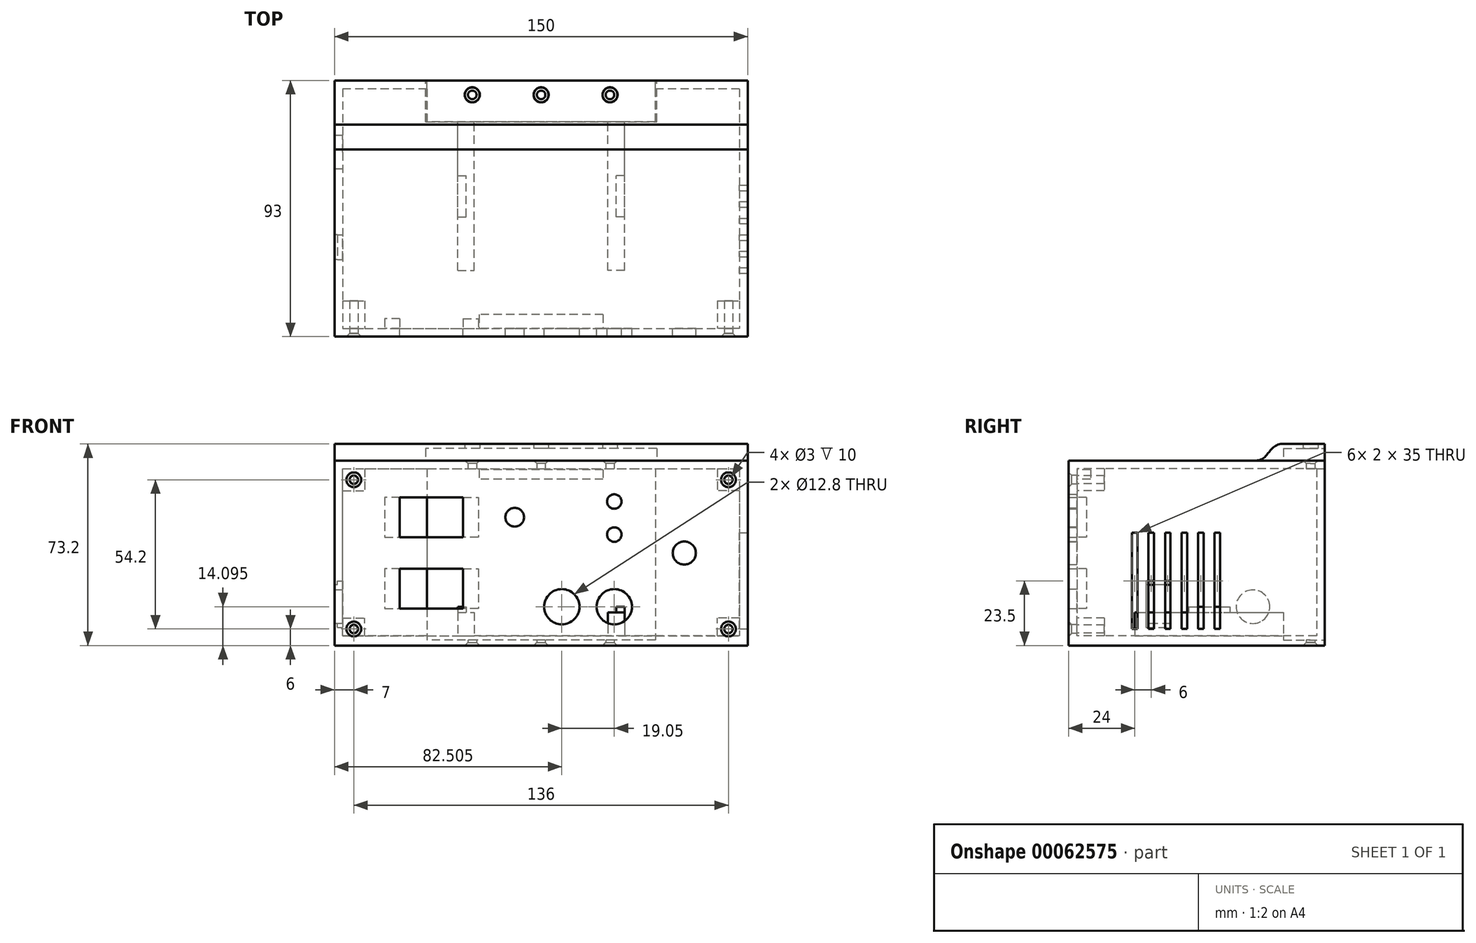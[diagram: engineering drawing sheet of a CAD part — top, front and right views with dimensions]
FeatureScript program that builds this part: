
annotation { "Feature Type Name" : "Feature", "Feature Type Description" : "" }
export const myFeature = defineFeature(function(context is Context, id is Id, definition is map)
    precondition{}
    {
        {
            var Q0;
            Q0=qCreatedBy(makeId("Top.planeOp"),FACE);
            var sketch = newSketch(context, id + "F0", { "sketchPlane" : qUnion([Q0])});
            skLineSegment(sketch, "E0.bottom", {"start": v(-75, 45) * mm, "end": v(75, 45) * mm});
            skLineSegment(sketch, "E0.top", {"start": v(-75, -45) * mm, "end": v(75, -45) * mm});
            skLineSegment(sketch, "E0.left", {"start": v(-75, 45) * mm, "end": v(-75, -45) * mm});
            skLineSegment(sketch, "E0.right", {"start": v(75, 45) * mm, "end": v(75, -45) * mm});
            skLineSegment(sketch, "E1", {"start": v(0, 0) * mm, "end": v(-75, 45) * mm, "construction": true});
            skLineSegment(sketch, "E2", {"start": v(0, 0) * mm, "end": v(-75, -45) * mm, "construction": true});
            skLineSegment(sketch, "E3", {"start": v(0, 0) * mm, "end": v(75, -45) * mm, "construction": true});
            skLineSegment(sketch, "E4", {"start": v(0, 0) * mm, "end": v(75, 45) * mm, "construction": true});
            skSolve(sketch);
        }
        {
            var Q0;
            Q0 = qSketchRegion(id + "F0", true);
            extrude(context, id + "F1", {"entities" : qUnion([Q0]), "depth" : 2 * mm});
        }
        {
            var Q0;
            Q0=makeQuery(id+"F1.opExtrude","CAP_FACE",FACE,{"disambiguationData":[OSD([sQuery(id+"F0.wireOp",EDGE,"E0.bottom"),sQuery(id+"F0.wireOp",EDGE,"E0.top"),sQuery(id+"F0.wireOp",EDGE,"E0.left"),sQuery(id+"F0.wireOp",EDGE,"E0.right")])],"isStart":false});
            var sketch = newSketch(context, id + "F2", { "sketchPlane" : qUnion([Q0])});
            skLineSegment(sketch, "E5.bottom", {"start": v(30.25, -24) * mm, "end": v(24.25, -24) * mm});
            skLineSegment(sketch, "E5.top", {"start": v(30.25, 30) * mm, "end": v(24.25, 30) * mm});
            skLineSegment(sketch, "E5.left", {"start": v(30.25, -24) * mm, "end": v(30.25, 30) * mm});
            skLineSegment(sketch, "E5.right", {"start": v(24.25, -24) * mm, "end": v(24.25, 30) * mm});
            skLineSegment(sketch, "E6.MirrorCS", {"start": v(-24.25, -24) * mm, "end": v(-24.25, 30) * mm});
            skLineSegment(sketch, "E7.MirrorCS", {"start": v(-30.25, -24) * mm, "end": v(-24.25, -24) * mm});
            skLineSegment(sketch, "E8.MirrorCS", {"start": v(-30.25, -24) * mm, "end": v(-30.25, 30) * mm});
            skLineSegment(sketch, "E9.MirrorCS", {"start": v(-30.25, 30) * mm, "end": v(-24.25, 30) * mm});
            skSolve(sketch);
        }
        {
            var Q0;
            Q0 = qSketchRegion(id + "F2", true);
            extrude(context, id + "F3", {"entities" : qUnion([Q0]), "operationType" : NewBodyOperationType.ADD, "depth" : (11.5 - 1.5) * mm});
        }
        {
            var Q0;
            Q0=makeQuery(id+"F3.opExtrude","CAP_FACE",FACE,{"disambiguationData":[OSD([sQuery(id+"F2.wireOp",EDGE,"E6.MirrorCS"),sQuery(id+"F2.wireOp",EDGE,"E7.MirrorCS"),sQuery(id+"F2.wireOp",EDGE,"E8.MirrorCS"),sQuery(id+"F2.wireOp",EDGE,"E9.MirrorCS")])],"isStart":false});
            var sketch = newSketch(context, id + "F4", { "sketchPlane" : qUnion([Q0])});
            skLineSegment(sketch, "E10.bottom", {"start": v(-30.25, -4.5) * mm, "end": v(-27.25, -4.5) * mm});
            skLineSegment(sketch, "E10.top", {"start": v(-30.25, 10.5) * mm, "end": v(-27.25, 10.5) * mm});
            skLineSegment(sketch, "E10.left", {"start": v(-30.25, -4.5) * mm, "end": v(-30.25, 10.5) * mm});
            skLineSegment(sketch, "E10.right", {"start": v(-27.25, -4.5) * mm, "end": v(-27.25, 10.5) * mm});
            skLineSegment(sketch, "E11", {"start": v(-30.25, 30) * mm, "end": v(-27.25, 10.5) * mm, "construction": true});
            skLineSegment(sketch, "E12", {"start": v(-27.25, -4.5) * mm, "end": v(-30.25, -24) * mm, "construction": true});
            skLineSegment(sketch, "E13.MirrorCS", {"start": v(27.25, -4.5) * mm, "end": v(27.25, 10.5) * mm});
            skLineSegment(sketch, "E14.MirrorCS", {"start": v(30.25, 10.5) * mm, "end": v(27.25, 10.5) * mm});
            skLineSegment(sketch, "E15.MirrorCS", {"start": v(30.25, -4.5) * mm, "end": v(30.25, 10.5) * mm});
            skLineSegment(sketch, "E16.MirrorCS", {"start": v(30.25, -4.5) * mm, "end": v(27.25, -4.5) * mm});
            skSolve(sketch);
        }
        {
            var Q0;
            Q0 = qSketchRegion(id + "F4", true);
            extrude(context, id + "F5", {"entities" : qUnion([Q0]), "operationType" : NewBodyOperationType.ADD, "depth" : 2 * mm});
        }
        {
            var Q0;
            Q0=makeQuery(id+"F1.opExtrude","CAP_FACE",FACE,{"disambiguationData":[OSD([sQuery(id+"F0.wireOp",EDGE,"E0.bottom"),sQuery(id+"F0.wireOp",EDGE,"E0.top"),sQuery(id+"F0.wireOp",EDGE,"E0.left"),sQuery(id+"F0.wireOp",EDGE,"E0.right")])],"isStart":true});
            var sketch = newSketch(context, id + "F6", { "sketchPlane" : qUnion([Q0])});
            skLineSegment(sketch, "E17", {"start": v(75, -39.8) * mm, "end": v(-75, -39.8) * mm, "construction": true});
            skPoint(sketch, "E18", {"position": v(0, -39.8) * mm});
            skPoint(sketch, "E19", {"position": v(25, -39.8) * mm});
            skPoint(sketch, "E20.MirrorP", {"position": v(-25, -39.8) * mm});
            skSolve(sketch);
        }
        {
            var Q0;
            Q0=makeQuery(id+"F1.opExtrude","SWEPT_FACE",FACE,{"disambiguationData":[OSD([sQuery(id+"F0.wireOp",EDGE,"E0.top")])]});
            var sketch = newSketch(context, id + "F7", { "sketchPlane" : qUnion([Q0])});
            skLineSegment(sketch, "E21", {"start": v(75, 2) * mm, "end": v(75, 67.2) * mm});
            skLineSegment(sketch, "E22", {"start": v(75, 67.2) * mm, "end": v(-75, 67.2) * mm});
            skLineSegment(sketch, "E23", {"start": v(-75, 67.2) * mm, "end": v(-75, 2) * mm});
            skLineSegment(sketch, "E24", {"start": v(-72, 2) * mm, "end": v(-72, 64.2) * mm});
            skLineSegment(sketch, "E25", {"start": v(-72, 64.2) * mm, "end": v(72, 64.2) * mm});
            skLineSegment(sketch, "E26", {"start": v(72, 64.2) * mm, "end": v(72, 2) * mm});
            skSolve(sketch);
        }
        {
            var Q0;
            {var subQ2=sQuery(id+"F7.wireOp",EDGE,"E21");Q0=makeQuery(id+"F7.imprint","IMPRINT",FACE,{"disambiguationData":[TD([[makeQuery(id+"F7.imprint","IMPRINT",EDGE,{"derivedFrom":subQ2}),1.0]])]});}
            var Q1;
            Q1=makeQuery(id+"F1.opExtrude","SWEPT_FACE",FACE,{"disambiguationData":[OSD([sQuery(id+"F0.wireOp",EDGE,"E0.bottom")])]});
            extrude(context, id + "F8", {"entities" : qUnion([Q0]), "operationType" : NewBodyOperationType.ADD, "endBound" : BoundingType.UP_TO_SURFACE, "oppositeDirection" : true, "endBoundEntityFace" : qUnion([Q1]), "depth" : 25 * mm});
        }
        {
            var Q0;
            Q0=makeQuery(id+"F8.boolean.opBoolean","MERGE",FACE,{"derivedFrom":[makeQuery(id+"F1.opExtrude","SWEPT_FACE",FACE,{"disambiguationData":[OSD([sQuery(id+"F0.wireOp",EDGE,"E0.bottom")])]}),makeQuery(id+"F8.opExtrude","CAP_FACE",FACE,{"disambiguationData":[OSD([sQuery(id+"F0.wireOp",EDGE,"E0.top"),sQuery(id+"F7.wireOp",EDGE,"E21"),sQuery(id+"F7.wireOp",EDGE,"E22"),sQuery(id+"F7.wireOp",EDGE,"E23"),sQuery(id+"F7.wireOp",EDGE,"E24"),sQuery(id+"F7.wireOp",EDGE,"E25"),sQuery(id+"F7.wireOp",EDGE,"E26")])],"isStart":false})]});
            var sketch = newSketch(context, id + "F9", { "sketchPlane" : qUnion([Q0])});
            skLineSegment(sketch, "E27.bottom", {"start": v(-75, 67.2) * mm, "end": v(75, 67.2) * mm});
            skLineSegment(sketch, "E27.top", {"start": v(-75, 0) * mm, "end": v(75, 0) * mm});
            skLineSegment(sketch, "E27.left", {"start": v(-75, 67.2) * mm, "end": v(-75, 0) * mm});
            skLineSegment(sketch, "E27.right", {"start": v(75, 67.2) * mm, "end": v(75, 0) * mm});
            skLineSegment(sketch, "E28.bottom", {"start": v(-41.5, 64.2) * mm, "end": v(41.5, 64.2) * mm});
            skLineSegment(sketch, "E28.top", {"start": v(-41.5, 2) * mm, "end": v(41.5, 2) * mm});
            skLineSegment(sketch, "E28.left", {"start": v(-41.5, 64.2) * mm, "end": v(-41.5, 2) * mm});
            skLineSegment(sketch, "E28.right", {"start": v(41.5, 64.2) * mm, "end": v(41.5, 2) * mm});
            skLineSegment(sketch, "E29", {"start": v(0, 5.83) * mm, "end": v(-41.5, 64.2) * mm, "construction": true});
            skLineSegment(sketch, "E30", {"start": v(0, 5.83) * mm, "end": v(41.5, 64.2) * mm, "construction": true});
            skSolve(sketch);
        }
        {
            var Q0;
            Q0 = qSketchRegion(id + "F9", true);
            extrude(context, id + "F10", {"entities" : qUnion([Q0]), "operationType" : NewBodyOperationType.ADD, "oppositeDirection" : true, "depth" : 3 * mm});
        }
        {
            var Q0;
            Q0=sQuery(id+"F6.wireOp",VERTEX,"E19");
            var Q1;
            Q1=sQuery(id+"F6.wireOp",VERTEX,"E18");
            var Q2;
            Q2=sQuery(id+"F6.wireOp",VERTEX,"E20.MirrorP");
            var Q3;
            Q3=makeQuery(id+"F1.opExtrude","SWEPT_BODY",BODY,{"disambiguationData":[OSD([sQuery(id+"F0.wireOp",EDGE,"E0.bottom"),sQuery(id+"F0.wireOp",EDGE,"E0.top"),sQuery(id+"F0.wireOp",EDGE,"E0.left"),sQuery(id+"F0.wireOp",EDGE,"E0.right")])]});
            hole(context, id + "F11", {"style" : HoleStyle.C_SINK, "holeDiameter" : 3.1 * mm, "cSinkDiameter" : 5.37 * mm, "endStyle" : HoleEndStyle.THROUGH, "locations" : qUnion([Q0, Q1, Q2]), "scope" : qUnion([Q3]), "cSinkAngle" : 90 * degree});
        }
        {
            var Q0;
            Q0=makeQuery(id+"F8.opExtrude","SWEPT_FACE",FACE,{"disambiguationData":[OSD([sQuery(id+"F7.wireOp",EDGE,"E22")])]});
            var sketch = newSketch(context, id + "F12", { "sketchPlane" : qUnion([Q0])});
            skPoint(sketch, "E31", {"position": v(0, 39.8) * mm});
            skPoint(sketch, "E32", {"position": v(-25, 39.8) * mm});
            skPoint(sketch, "E33", {"position": v(25, 39.8) * mm});
            skSolve(sketch);
        }
        {
            var Q0;
            Q0=sQuery(id+"F12.wireOp",VERTEX,"E32");
            var Q1;
            Q1=sQuery(id+"F12.wireOp",VERTEX,"E31");
            var Q2;
            Q2=sQuery(id+"F12.wireOp",VERTEX,"E33");
            var Q3;
            Q3=makeQuery(id+"F1.opExtrude","SWEPT_BODY",BODY,{"disambiguationData":[OSD([sQuery(id+"F0.wireOp",EDGE,"E0.bottom"),sQuery(id+"F0.wireOp",EDGE,"E0.top"),sQuery(id+"F0.wireOp",EDGE,"E0.left"),sQuery(id+"F0.wireOp",EDGE,"E0.right")])]});
            hole(context, id + "F13", {"style" : HoleStyle.C_SINK, "holeDiameter" : 3.1 * mm, "cSinkDiameter" : 5.37 * mm, "endStyle" : HoleEndStyle.THROUGH, "locations" : qUnion([Q0, Q1, Q2]), "scope" : qUnion([Q3]), "cSinkAngle" : 90 * degree});
        }
        {
            var Q0;
            Q0=makeQuery(id+"F8.boolean.opBoolean","MERGE",FACE,{"derivedFrom":[makeQuery(id+"F1.opExtrude","SWEPT_FACE",FACE,{"disambiguationData":[OSD([sQuery(id+"F0.wireOp",EDGE,"E0.left")])]}),makeQuery(id+"F8.opExtrude","SWEPT_FACE",FACE,{"disambiguationData":[OSD([sQuery(id+"F7.wireOp",EDGE,"E23")])]})]});
            var sketch = newSketch(context, id + "F14", { "sketchPlane" : qUnion([Q0])});
            skPoint(sketch, "E34", {"position": v(-18.9, 14.1) * mm});
            skLineSegment(sketch, "E35.bottom", {"start": v(11, 22) * mm, "end": v(20, 22) * mm});
            skLineSegment(sketch, "E35.top", {"start": v(11, 8) * mm, "end": v(20, 8) * mm});
            skLineSegment(sketch, "E35.left", {"start": v(11, 22) * mm, "end": v(11, 8) * mm});
            skLineSegment(sketch, "E35.right", {"start": v(20, 22) * mm, "end": v(20, 8) * mm});
            skSolve(sketch);
        }
        {
            var Q0;
            Q0=sQuery(id+"F14.wireOp",VERTEX,"E34");
            var Q1;
            Q1=makeQuery(id+"F1.opExtrude","SWEPT_BODY",BODY,{"disambiguationData":[OSD([sQuery(id+"F0.wireOp",EDGE,"E0.bottom"),sQuery(id+"F0.wireOp",EDGE,"E0.top"),sQuery(id+"F0.wireOp",EDGE,"E0.left"),sQuery(id+"F0.wireOp",EDGE,"E0.right")])]});
            hole(context, id + "F15", {"style" : HoleStyle.SIMPLE, "holeDiameter" : 12.2 * mm, "endStyle" : HoleEndStyle.BLIND, "holeDepth" : 20 * mm, "locations" : qUnion([Q0]), "scope" : qUnion([Q1])});
        }
        {
            var Q0;
            Q0=makeQuery(id+"F14.imprint","IMPRINT",FACE,{"disambiguationData":[TD([[makeQuery(id+"F14.imprint","IMPRINT",EDGE,{"derivedFrom":sQuery(id+"F14.wireOp",EDGE,"E35.bottom")}),-1.0]])]});
            extrude(context, id + "F16", {"entities" : qUnion([Q0]), "operationType" : NewBodyOperationType.REMOVE, "endBound" : BoundingType.UP_TO_NEXT, "oppositeDirection" : true, "depth" : 25 * mm});
        }
        {
            var Q0;
            Q0=makeQuery(id+"F8.opExtrude","SWEPT_FACE",FACE,{"disambiguationData":[OSD([sQuery(id+"F7.wireOp",EDGE,"E24")])]});
            var sketch = newSketch(context, id + "F17", { "sketchPlane" : qUnion([Q0])});
            skLineSegment(sketch, "E36", {"start": v(-11, 22) * mm, "end": v(-11, 23.5) * mm});
            skLineSegment(sketch, "E37", {"start": v(-11, 23.5) * mm, "end": v(-20, 23.5) * mm});
            skLineSegment(sketch, "E38", {"start": v(-20, 23.5) * mm, "end": v(-20, 22) * mm});
            skLineSegment(sketch, "E39", {"start": v(-20, 8) * mm, "end": v(-20, 6.5) * mm});
            skLineSegment(sketch, "E40", {"start": v(-20, 6.5) * mm, "end": v(-11, 6.5) * mm});
            skLineSegment(sketch, "E41", {"start": v(-11, 6.5) * mm, "end": v(-11, 8) * mm});
            skSolve(sketch);
        }
        {
            var Q0;
            Q0=makeQuery(id+"F17.imprint","IMPRINT",FACE,{"disambiguationData":[TD([[makeQuery(id+"F17.imprint","IMPRINT",EDGE,{"derivedFrom":sQuery(id+"F17.wireOp",EDGE,"E39")}),1.0]])]});
            var Q1;
            Q1=makeQuery(id+"F17.imprint","IMPRINT",FACE,{"disambiguationData":[TD([[makeQuery(id+"F17.imprint","IMPRINT",EDGE,{"derivedFrom":sQuery(id+"F17.wireOp",EDGE,"E36")}),1.0]])]});
            extrude(context, id + "F18", {"entities" : qUnion([Q0, Q1]), "operationType" : NewBodyOperationType.REMOVE, "oppositeDirection" : true, "depth" : 2 * mm});
        }
        {
            var Q0;
            Q0=makeQuery(id+"F8.boolean.opBoolean","MERGE",FACE,{"derivedFrom":[makeQuery(id+"F1.opExtrude","SWEPT_FACE",FACE,{"disambiguationData":[OSD([sQuery(id+"F0.wireOp",EDGE,"E0.right")])]}),makeQuery(id+"F8.opExtrude","SWEPT_FACE",FACE,{"disambiguationData":[OSD([sQuery(id+"F7.wireOp",EDGE,"E21")])]})]});
            var sketch = newSketch(context, id + "F19", { "sketchPlane" : qUnion([Q0])});
            skLineSegment(sketch, "E42.bottom", {"start": v(-25, 6) * mm, "end": v(-23, 6) * mm});
            skLineSegment(sketch, "E42.top", {"start": v(-25, 41) * mm, "end": v(-23, 41) * mm});
            skLineSegment(sketch, "E42.left", {"start": v(-25, 6) * mm, "end": v(-25, 41) * mm});
            skLineSegment(sketch, "E42.right", {"start": v(-23, 6) * mm, "end": v(-23, 41) * mm});
            skLineSegment(sketch, "E43.1.0.0", {"start": v(-17, 6) * mm, "end": v(-17, 41) * mm});
            skLineSegment(sketch, "E43.1.0.1", {"start": v(-19, 6) * mm, "end": v(-19, 41) * mm});
            skLineSegment(sketch, "E43.1.0.2", {"start": v(-19, 41) * mm, "end": v(-17, 41) * mm});
            skLineSegment(sketch, "E43.1.0.3", {"start": v(-19, 6) * mm, "end": v(-17, 6) * mm});
            skLineSegment(sketch, "E43.2.0.0", {"start": v(-11, 6) * mm, "end": v(-11, 41) * mm});
            skLineSegment(sketch, "E43.2.0.1", {"start": v(-13, 6) * mm, "end": v(-13, 41) * mm});
            skLineSegment(sketch, "E43.2.0.2", {"start": v(-13, 41) * mm, "end": v(-11, 41) * mm});
            skLineSegment(sketch, "E43.2.0.3", {"start": v(-13, 6) * mm, "end": v(-11, 6) * mm});
            skLineSegment(sketch, "E43.3.0.0", {"start": v(-5, 6) * mm, "end": v(-5, 41) * mm});
            skLineSegment(sketch, "E43.3.0.1", {"start": v(-7, 6) * mm, "end": v(-7, 41) * mm});
            skLineSegment(sketch, "E43.3.0.2", {"start": v(-7, 41) * mm, "end": v(-5, 41) * mm});
            skLineSegment(sketch, "E43.3.0.3", {"start": v(-7, 6) * mm, "end": v(-5, 6) * mm});
            skLineSegment(sketch, "E43.4.0.0", {"start": v(1, 6) * mm, "end": v(1, 41) * mm});
            skLineSegment(sketch, "E43.4.0.1", {"start": v(-1, 6) * mm, "end": v(-1, 41) * mm});
            skLineSegment(sketch, "E43.4.0.2", {"start": v(-1, 41) * mm, "end": v(1, 41) * mm});
            skLineSegment(sketch, "E43.4.0.3", {"start": v(-1, 6) * mm, "end": v(1, 6) * mm});
            skLineSegment(sketch, "E43.5.0.0", {"start": v(7, 6) * mm, "end": v(7, 41) * mm});
            skLineSegment(sketch, "E43.5.0.1", {"start": v(5, 6) * mm, "end": v(5, 41) * mm});
            skLineSegment(sketch, "E43.5.0.2", {"start": v(5, 41) * mm, "end": v(7, 41) * mm});
            skLineSegment(sketch, "E43.5.0.3", {"start": v(5, 6) * mm, "end": v(7, 6) * mm});
            skLineSegment(sketch, "E43.direction1", {"start": v(-43, 6) * mm, "end": v(-37, 6) * mm, "construction": true});
            skSolve(sketch);
        }
        {
            var Q0;
            Q0=makeQuery(id+"F19.imprint","IMPRINT",FACE,{"disambiguationData":[TD([[makeQuery(id+"F19.imprint","IMPRINT",EDGE,{"derivedFrom":sQuery(id+"F19.wireOp",EDGE,"E42.bottom")}),1.0]])]});
            var Q1;
            Q1=makeQuery(id+"F19.imprint","IMPRINT",FACE,{"disambiguationData":[TD([[makeQuery(id+"F19.imprint","IMPRINT",EDGE,{"derivedFrom":sQuery(id+"F19.wireOp",EDGE,"E43.1.0.0")}),1.0]])]});
            var Q2;
            Q2=makeQuery(id+"F19.imprint","IMPRINT",FACE,{"disambiguationData":[TD([[makeQuery(id+"F19.imprint","IMPRINT",EDGE,{"derivedFrom":sQuery(id+"F19.wireOp",EDGE,"E43.2.0.0")}),1.0]])]});
            var Q3;
            Q3=makeQuery(id+"F19.imprint","IMPRINT",FACE,{"disambiguationData":[TD([[makeQuery(id+"F19.imprint","IMPRINT",EDGE,{"derivedFrom":sQuery(id+"F19.wireOp",EDGE,"E43.3.0.0")}),1.0]])]});
            var Q4;
            Q4=makeQuery(id+"F19.imprint","IMPRINT",FACE,{"disambiguationData":[TD([[makeQuery(id+"F19.imprint","IMPRINT",EDGE,{"derivedFrom":sQuery(id+"F19.wireOp",EDGE,"E43.4.0.0")}),1.0]])]});
            var Q5;
            Q5=makeQuery(id+"F19.imprint","IMPRINT",FACE,{"disambiguationData":[TD([[makeQuery(id+"F19.imprint","IMPRINT",EDGE,{"derivedFrom":sQuery(id+"F19.wireOp",EDGE,"E43.5.0.0")}),1.0]])]});
            extrude(context, id + "F20", {"entities" : qUnion([Q0, Q1, Q2, Q3, Q4, Q5]), "operationType" : NewBodyOperationType.REMOVE, "endBound" : BoundingType.UP_TO_NEXT, "oppositeDirection" : true, "depth" : 25 * mm});
        }
        {
            var Q0;
            {var subQ0=sQuery(id+"F0.wireOp",EDGE,"E0.top");Q0=makeQuery(id+"F8.boolean.opBoolean","MERGE",FACE,{"derivedFrom":[makeQuery(id+"F1.opExtrude","SWEPT_FACE",FACE,{"disambiguationData":[OSD([subQ0])]}),makeQuery(id+"F8.opExtrude","CAP_FACE",FACE,{"disambiguationData":[OSD([subQ0,sQuery(id+"F7.wireOp",EDGE,"E21"),sQuery(id+"F7.wireOp",EDGE,"E22"),sQuery(id+"F7.wireOp",EDGE,"E23"),sQuery(id+"F7.wireOp",EDGE,"E24"),sQuery(id+"F7.wireOp",EDGE,"E25"),sQuery(id+"F7.wireOp",EDGE,"E26")])],"isStart":true})]});}
            var sketch = newSketch(context, id + "F21", { "sketchPlane" : qUnion([Q0])});
            skLineSegment(sketch, "E44.bottom", {"start": v(-75, 67.2) * mm, "end": v(-64, 67.2) * mm});
            skLineSegment(sketch, "E44.top", {"start": v(-75, 56.2) * mm, "end": v(-64, 56.2) * mm});
            skLineSegment(sketch, "E44.left", {"start": v(-75, 67.2) * mm, "end": v(-75, 56.2) * mm});
            skLineSegment(sketch, "E44.right", {"start": v(-64, 67.2) * mm, "end": v(-64, 56.2) * mm});
            skLineSegment(sketch, "E45", {"start": v(-72, 64.2) * mm, "end": v(-64, 56.2) * mm, "construction": true});
            skPoint(sketch, "E46", {"position": v(-68, 60.2) * mm});
            skLineSegment(sketch, "E47.MirrorCS", {"start": v(75, 67.2) * mm, "end": v(75, 56.2) * mm});
            skLineSegment(sketch, "E48.MirrorCS", {"start": v(75, 67.2) * mm, "end": v(64, 67.2) * mm});
            skLineSegment(sketch, "E49.MirrorCS", {"start": v(75, 56.2) * mm, "end": v(64, 56.2) * mm});
            skLineSegment(sketch, "E50.MirrorCS", {"start": v(64, 67.2) * mm, "end": v(64, 56.2) * mm});
            skPoint(sketch, "E51.MirrorP", {"position": v(68, 60.2) * mm});
            skLineSegment(sketch, "E52", {"start": v(-75, 33.6) * mm, "end": v(75, 33.6) * mm, "construction": true});
            skLineSegment(sketch, "E53.bottom", {"start": v(-75, 0) * mm, "end": v(-64, 0) * mm});
            skLineSegment(sketch, "E53.top", {"start": v(-75, 10) * mm, "end": v(-64, 10) * mm});
            skLineSegment(sketch, "E53.left", {"start": v(-75, 0) * mm, "end": v(-75, 10) * mm});
            skLineSegment(sketch, "E53.right", {"start": v(-64, 0) * mm, "end": v(-64, 10) * mm});
            skLineSegment(sketch, "E54", {"start": v(-64, 10) * mm, "end": v(-72, 2) * mm, "construction": true});
            skPoint(sketch, "E55", {"position": v(-68, 6) * mm});
            skPoint(sketch, "E56.MirrorP", {"position": v(68, 6) * mm});
            skLineSegment(sketch, "E57.MirrorCS", {"start": v(75, 0) * mm, "end": v(64, 0) * mm});
            skLineSegment(sketch, "E58.MirrorCS", {"start": v(64, 0) * mm, "end": v(64, 10) * mm});
            skLineSegment(sketch, "E59.MirrorCS", {"start": v(75, 10) * mm, "end": v(64, 10) * mm});
            skLineSegment(sketch, "E60.MirrorCS", {"start": v(75, 0) * mm, "end": v(75, 10) * mm});
            skSolve(sketch);
        }
        {
            var Q0;
            {var subQ0=sQuery(id+"F21.wireOp",EDGE,"E53.right");var subQ1=sQuery(id+"F21.wireOp",EDGE,"E53.top");var subQ2=makeQuery(id+"F21.imprint","INTERSECT",VERTEX,{"derivedFrom":[subQ1,subQ0]});Q0=makeQuery(id+"F21.imprint","IMPRINT",FACE,{"disambiguationData":[TD([[makeQuery(id+"F21.imprint","IMPRINT",EDGE,{"disambiguationData":[TD([[subQ2,1.0]])],"derivedFrom":subQ1}),-1.0]])]});}
            var Q1;
            {var subQ0=sQuery(id+"F21.wireOp",EDGE,"E44.right");var subQ1=sQuery(id+"F21.wireOp",EDGE,"E44.top");var subQ2=makeQuery(id+"F21.imprint","INTERSECT",VERTEX,{"derivedFrom":[subQ1,subQ0]});Q1=makeQuery(id+"F21.imprint","IMPRINT",FACE,{"disambiguationData":[TD([[makeQuery(id+"F21.imprint","IMPRINT",EDGE,{"disambiguationData":[TD([[subQ2,1.0]])],"derivedFrom":subQ1}),1.0]])]});}
            var Q2;
            {var subQ0=sQuery(id+"F21.wireOp",EDGE,"E50.MirrorCS");var subQ1=sQuery(id+"F21.wireOp",EDGE,"E49.MirrorCS");var subQ2=makeQuery(id+"F21.imprint","INTERSECT",VERTEX,{"derivedFrom":[subQ1,subQ0]});Q2=makeQuery(id+"F21.imprint","IMPRINT",FACE,{"disambiguationData":[TD([[makeQuery(id+"F21.imprint","IMPRINT",EDGE,{"disambiguationData":[TD([[subQ2,1.0]])],"derivedFrom":subQ1}),-1.0]])]});}
            var Q3;
            {var subQ0=sQuery(id+"F21.wireOp",EDGE,"E59.MirrorCS");var subQ1=sQuery(id+"F21.wireOp",EDGE,"E58.MirrorCS");var subQ2=makeQuery(id+"F21.imprint","INTERSECT",VERTEX,{"derivedFrom":[subQ1,subQ0]});Q3=makeQuery(id+"F21.imprint","IMPRINT",FACE,{"disambiguationData":[TD([[makeQuery(id+"F21.imprint","IMPRINT",EDGE,{"disambiguationData":[TD([[subQ2,1.0]])],"derivedFrom":subQ1}),-1.0]])]});}
            extrude(context, id + "F22", {"entities" : qUnion([Q0, Q1, Q2, Q3]), "operationType" : NewBodyOperationType.ADD, "oppositeDirection" : true, "depth" : 10 * mm});
        }
        {
            var Q0;
            Q0=sQuery(id+"F21.wireOp",VERTEX,"E46");
            var Q1;
            Q1=sQuery(id+"F21.wireOp",VERTEX,"E51.MirrorP");
            var Q2;
            Q2=sQuery(id+"F21.wireOp",VERTEX,"E56.MirrorP");
            var Q3;
            Q3=sQuery(id+"F21.wireOp",VERTEX,"E55");
            var Q4;
            Q4=makeQuery(id+"F1.opExtrude","SWEPT_BODY",BODY,{"disambiguationData":[OSD([sQuery(id+"F0.wireOp",EDGE,"E0.bottom"),sQuery(id+"F0.wireOp",EDGE,"E0.top"),sQuery(id+"F0.wireOp",EDGE,"E0.left"),sQuery(id+"F0.wireOp",EDGE,"E0.right")])]});
            hole(context, id + "F23", {"style" : HoleStyle.SIMPLE, "holeDiameter" : 3 * mm, "endStyle" : HoleEndStyle.BLIND, "holeDepth" : 20 * mm, "locations" : qUnion([Q0, Q1, Q2, Q3]), "scope" : qUnion([Q4])});
        }
        {
            var Q0;
            {var subQ1=sQuery(id+"F21.wireOp",EDGE,"E44.bottom");Q0=makeQuery(id+"F21.imprint","IMPRINT",FACE,{"disambiguationData":[TD([[makeQuery(id+"F21.imprint","IMPRINT",EDGE,{"derivedFrom":subQ1}),1.0]])]});}
            var sketch = newSketch(context, id + "F24", { "sketchPlane" : qUnion([Q0])});
            skLineSegment(sketch, "E61.bottom", {"start": v(-75, 67.2) * mm, "end": v(75, 67.2) * mm});
            skLineSegment(sketch, "E61.top", {"start": v(-75, 0) * mm, "end": v(75, 0) * mm});
            skLineSegment(sketch, "E61.left", {"start": v(-75, 67.2) * mm, "end": v(-75, 0) * mm});
            skLineSegment(sketch, "E61.right", {"start": v(75, 67.2) * mm, "end": v(75, 0) * mm});
            skLineSegment(sketch, "E62.bottom", {"start": v(-51.3, 53.84) * mm, "end": v(-28.3, 53.84) * mm});
            skLineSegment(sketch, "E62.top", {"start": v(-51.3, 39.34) * mm, "end": v(-28.3, 39.34) * mm});
            skLineSegment(sketch, "E62.left", {"start": v(-51.3, 53.84) * mm, "end": v(-51.3, 39.34) * mm});
            skLineSegment(sketch, "E62.right", {"start": v(-28.3, 53.84) * mm, "end": v(-28.3, 39.34) * mm});
            skLineSegment(sketch, "E63", {"start": v(-51.3, 53.84) * mm, "end": v(-56.8, 53.84) * mm});
            skLineSegment(sketch, "E64", {"start": v(-56.8, 53.84) * mm, "end": v(-56.8, 39.34) * mm});
            skLineSegment(sketch, "E65", {"start": v(-56.8, 39.34) * mm, "end": v(-51.3, 39.34) * mm});
            skLineSegment(sketch, "E66", {"start": v(-28.3, 53.84) * mm, "end": v(-22.8, 53.84) * mm});
            skLineSegment(sketch, "E67", {"start": v(-22.8, 53.84) * mm, "end": v(-22.8, 39.34) * mm});
            skLineSegment(sketch, "E68", {"start": v(-22.8, 39.34) * mm, "end": v(-28.3, 39.34) * mm});
            skLineSegment(sketch, "E69.left", {"start": v(-51.3, 27.86) * mm, "end": v(-51.3, 13.36) * mm});
            skLineSegment(sketch, "E69.top", {"start": v(-51.3, 13.36) * mm, "end": v(-28.3, 13.36) * mm});
            skLineSegment(sketch, "E70", {"start": v(-51.3, 27.86) * mm, "end": v(-56.8, 27.86) * mm});
            skLineSegment(sketch, "E69.right", {"start": v(-28.3, 27.86) * mm, "end": v(-28.3, 13.36) * mm});
            skLineSegment(sketch, "E71", {"start": v(-56.8, 13.36) * mm, "end": v(-51.3, 13.36) * mm});
            skLineSegment(sketch, "E69.bottom", {"start": v(-51.3, 27.86) * mm, "end": v(-28.3, 27.86) * mm});
            skLineSegment(sketch, "E72", {"start": v(-56.8, 27.86) * mm, "end": v(-56.8, 13.36) * mm});
            skLineSegment(sketch, "E73", {"start": v(-22.8, 27.86) * mm, "end": v(-22.8, 13.36) * mm});
            skLineSegment(sketch, "E74", {"start": v(-28.3, 27.86) * mm, "end": v(-22.8, 27.86) * mm});
            skLineSegment(sketch, "E75", {"start": v(-22.8, 13.36) * mm, "end": v(-28.3, 13.36) * mm});
            skLineSegment(sketch, "E76", {"start": v(-56.8, 67.2) * mm, "end": v(-56.8, 0) * mm, "construction": true});
            skCircle(sketch, "E77", {"center": v(7.5, 14.1) * mm, "radius": 6.4 * mm});
            skCircle(sketch, "E78", {"center": v(26.55, 14.1) * mm, "radius": 6.4 * mm});
            skLineSegment(sketch, "E79", {"start": v(-75, 14.1) * mm, "end": v(75, 14.1) * mm, "construction": true});
            skCircle(sketch, "E80", {"center": v(26.55, 52.3) * mm, "radius": 2.62 * mm});
            skCircle(sketch, "E81", {"center": v(26.55, 40.3) * mm, "radius": 2.62 * mm});
            skLineSegment(sketch, "E82", {"start": v(26.55, 0) * mm, "end": v(26.55, 67.2) * mm, "construction": true});
            skCircle(sketch, "E83", {"center": v(51.96, 33.6) * mm, "radius": 4.2 * mm});
            skCircle(sketch, "E84", {"center": v(51.96, 33.6) * mm, "radius": 14 * mm, "construction": true});
            skLineSegment(sketch, "E85", {"start": v(-39.8, 27.86) * mm, "end": v(-39.8, 33.6) * mm, "construction": true});
            skPoint(sketch, "E85.endSnap0", {"position": v(-56.8, 33.6) * mm});
            skLineSegment(sketch, "E86", {"start": v(-39.8, 33.6) * mm, "end": v(-39.8, 39.34) * mm, "construction": true});
            skCircle(sketch, "E87", {"center": v(-9.58, 46.59) * mm, "radius": 3.4 * mm});
            skLineSegment(sketch, "E88", {"start": v(-56.8, 46.59) * mm, "end": v(75, 46.59) * mm, "construction": true});
            skSolve(sketch);
        }
        {
            var Q0;
            {var subQ1=makeQuery(id+"F8.opExtrude","CAP_EDGE",EDGE,{"disambiguationData":[OSD([sQuery(id+"F7.wireOp",EDGE,"E25")])],"isStart":true});var subQ5=makeQuery(id+"F8.opExtrude","CAP_EDGE",EDGE,{"disambiguationData":[OSD([sQuery(id+"F7.wireOp",EDGE,"E24")])],"isStart":true});var subQ11=makeQuery(id+"F21.imprint","INTERSECT",VERTEX,{"derivedFrom":[subQ5,subQ1]});Q0=makeQuery(id+"F24.imprint","IMPRINT",FACE,{"disambiguationData":[TD([[makeQuery(id+"F24.imprint","IMPRINT",EDGE,{"derivedFrom":makeQuery(id+"F21.imprint","IMPRINT",EDGE,{"disambiguationData":[TD([[subQ11,1.0]])],"derivedFrom":subQ5})}),1.0]])]});}
            var Q1;
            {var subQ6=sQuery(id+"F24.wireOp",EDGE,"E61.top");Q1=makeQuery(id+"F24.imprint","IMPRINT",FACE,{"disambiguationData":[TD([[makeQuery(id+"F24.imprint","IMPRINT",EDGE,{"derivedFrom":subQ6}),1.0]])]});}
            var Q2;
            Q2=makeQuery(id+"F24.imprint","IMPRINT",FACE,{"disambiguationData":[TD([[makeQuery(id+"F24.imprint","IMPRINT",EDGE,{"derivedFrom":sQuery(id+"F24.wireOp",EDGE,"E62.right")}),1.0]])]});
            var Q3;
            Q3=makeQuery(id+"F24.imprint","IMPRINT",FACE,{"disambiguationData":[TD([[makeQuery(id+"F24.imprint","IMPRINT",EDGE,{"derivedFrom":sQuery(id+"F24.wireOp",EDGE,"E69.right")}),1.0]])]});
            var Q4;
            Q4=makeQuery(id+"F24.imprint","IMPRINT",FACE,{"disambiguationData":[TD([[makeQuery(id+"F24.imprint","IMPRINT",EDGE,{"derivedFrom":sQuery(id+"F24.wireOp",EDGE,"E69.left")}),-1.0]])]});
            var Q5;
            Q5=makeQuery(id+"F24.imprint","IMPRINT",FACE,{"disambiguationData":[TD([[makeQuery(id+"F24.imprint","IMPRINT",EDGE,{"derivedFrom":sQuery(id+"F24.wireOp",EDGE,"E62.left")}),-1.0]])]});
            extrude(context, id + "F25", {"entities" : qUnion([Q0, Q1, Q2, Q3, Q4, Q5]), "depth" : 3 * mm});
        }
        {
            var Q0;
            Q0=makeQuery(id+"F24.imprint","IMPRINT",FACE,{"disambiguationData":[TD([[makeQuery(id+"F24.imprint","IMPRINT",EDGE,{"derivedFrom":sQuery(id+"F24.wireOp",EDGE,"E62.right")}),1.0]])]});
            var Q1;
            Q1=makeQuery(id+"F24.imprint","IMPRINT",FACE,{"disambiguationData":[TD([[makeQuery(id+"F24.imprint","IMPRINT",EDGE,{"derivedFrom":sQuery(id+"F24.wireOp",EDGE,"E62.left")}),-1.0]])]});
            var Q2;
            Q2=makeQuery(id+"F24.imprint","IMPRINT",FACE,{"disambiguationData":[TD([[makeQuery(id+"F24.imprint","IMPRINT",EDGE,{"derivedFrom":sQuery(id+"F24.wireOp",EDGE,"E69.left")}),-1.0]])]});
            var Q3;
            Q3=makeQuery(id+"F24.imprint","IMPRINT",FACE,{"disambiguationData":[TD([[makeQuery(id+"F24.imprint","IMPRINT",EDGE,{"derivedFrom":sQuery(id+"F24.wireOp",EDGE,"E69.right")}),1.0]])]});
            extrude(context, id + "F26", {"entities" : qUnion([Q0, Q1, Q2, Q3]), "operationType" : NewBodyOperationType.ADD, "oppositeDirection" : true, "depth" : 3.5 * mm});
        }
        {
            var Q0;
            Q0=makeQuery(id+"F25.opExtrude","CAP_FACE",FACE,{"disambiguationData":[OSD([sQuery(id+"F24.wireOp",EDGE,"E61.bottom"),sQuery(id+"F24.wireOp",EDGE,"E61.top"),sQuery(id+"F24.wireOp",EDGE,"E61.left"),sQuery(id+"F24.wireOp",EDGE,"E61.right"),sQuery(id+"F24.wireOp",EDGE,"E62.bottom"),sQuery(id+"F24.wireOp",EDGE,"E62.top"),sQuery(id+"F24.wireOp",EDGE,"E62.left"),sQuery(id+"F24.wireOp",EDGE,"E62.right"),sQuery(id+"F24.wireOp",EDGE,"E69.left"),sQuery(id+"F24.wireOp",EDGE,"E69.top"),sQuery(id+"F24.wireOp",EDGE,"E69.right"),sQuery(id+"F24.wireOp",EDGE,"E69.bottom"),sQuery(id+"F24.wireOp",EDGE,"E77"),sQuery(id+"F24.wireOp",EDGE,"E78"),sQuery(id+"F24.wireOp",EDGE,"E80"),sQuery(id+"F24.wireOp",EDGE,"E81"),sQuery(id+"F24.wireOp",EDGE,"E83")])],"isStart":false});
            var sketch = newSketch(context, id + "F27", { "sketchPlane" : qUnion([Q0])});
            skPoint(sketch, "E89", {"position": v(-68, 60.2) * mm});
            skPoint(sketch, "E90", {"position": v(-68, 6) * mm});
            skPoint(sketch, "E91", {"position": v(68, 6) * mm});
            skPoint(sketch, "E92", {"position": v(68, 60.2) * mm});
            skSolve(sketch);
        }
        {
            var Q0;
            Q0=sQuery(id+"F27.wireOp",VERTEX,"E89");
            var Q1;
            Q1=sQuery(id+"F27.wireOp",VERTEX,"E90");
            var Q2;
            Q2=sQuery(id+"F27.wireOp",VERTEX,"E91");
            var Q3;
            Q3=sQuery(id+"F27.wireOp",VERTEX,"E92");
            var Q4;
            Q4=makeQuery(id+"F25.opExtrude","SWEPT_BODY",BODY,{"disambiguationData":[OSD([sQuery(id+"F24.wireOp",EDGE,"E61.bottom"),sQuery(id+"F24.wireOp",EDGE,"E61.top"),sQuery(id+"F24.wireOp",EDGE,"E61.left"),sQuery(id+"F24.wireOp",EDGE,"E61.right"),sQuery(id+"F24.wireOp",EDGE,"E62.bottom"),sQuery(id+"F24.wireOp",EDGE,"E62.top"),sQuery(id+"F24.wireOp",EDGE,"E62.left"),sQuery(id+"F24.wireOp",EDGE,"E62.right"),sQuery(id+"F24.wireOp",EDGE,"E69.left"),sQuery(id+"F24.wireOp",EDGE,"E69.top"),sQuery(id+"F24.wireOp",EDGE,"E69.right"),sQuery(id+"F24.wireOp",EDGE,"E69.bottom"),sQuery(id+"F24.wireOp",EDGE,"E77"),sQuery(id+"F24.wireOp",EDGE,"E78"),sQuery(id+"F24.wireOp",EDGE,"E80"),sQuery(id+"F24.wireOp",EDGE,"E81"),sQuery(id+"F24.wireOp",EDGE,"E83")])]});
            hole(context, id + "F28", {"style" : HoleStyle.C_SINK, "holeDiameter" : 3.1 * mm, "cSinkDiameter" : 5.37 * mm, "endStyle" : HoleEndStyle.THROUGH, "locations" : qUnion([Q0, Q1, Q2, Q3]), "scope" : qUnion([Q4]), "cSinkAngle" : 90 * degree});
        }
        {
            var Q0;
            Q0=makeQuery(id+"F1.opExtrude","CAP_FACE",FACE,{"disambiguationData":[OSD([sQuery(id+"F0.wireOp",EDGE,"E0.bottom"),sQuery(id+"F0.wireOp",EDGE,"E0.top"),sQuery(id+"F0.wireOp",EDGE,"E0.left"),sQuery(id+"F0.wireOp",EDGE,"E0.right")])],"isStart":false});
            var sketch = newSketch(context, id + "F29", { "sketchPlane" : qUnion([Q0])});
            skLineSegment(sketch, "E93", {"start": v(64, -45) * mm, "end": v(64, -35) * mm});
            skLineSegment(sketch, "E94", {"start": v(64, -35) * mm, "end": v(72, -35) * mm});
            skLineSegment(sketch, "E95", {"start": v(72, -35) * mm, "end": v(72, 42) * mm});
            skLineSegment(sketch, "E96", {"start": v(72, 42) * mm, "end": v(41.5, 42) * mm});
            skLineSegment(sketch, "E97", {"start": v(30.25, 30) * mm, "end": v(-30.25, 30) * mm});
            skLineSegment(sketch, "E98", {"start": v(-41.5, 42) * mm, "end": v(-72, 42) * mm});
            skLineSegment(sketch, "E99", {"start": v(-72, 42) * mm, "end": v(-72, -35) * mm});
            skLineSegment(sketch, "E100", {"start": v(-72, -35) * mm, "end": v(-64, -35) * mm});
            skLineSegment(sketch, "E101", {"start": v(-64, -35) * mm, "end": v(-64, -45) * mm});
            skLineSegment(sketch, "E102", {"start": v(-64, -45) * mm, "end": v(64, -45) * mm});
            skLineSegment(sketch, "E103", {"start": v(-41.5, 42) * mm, "end": v(-41.5, -45) * mm, "construction": true});
            skLineSegment(sketch, "E104", {"start": v(-30.25, 30) * mm, "end": v(-72, 30) * mm, "construction": true});
            skLineSegment(sketch, "E105", {"start": v(-41.5, 42) * mm, "end": v(-41.5, 30) * mm});
            skLineSegment(sketch, "E106", {"start": v(30.25, 30) * mm, "end": v(72, 30) * mm, "construction": true});
            skLineSegment(sketch, "E107", {"start": v(41.5, 42) * mm, "end": v(41.5, 30) * mm});
            skLineSegment(sketch, "E108", {"start": v(41.5, 30) * mm, "end": v(30.25, 30) * mm});
            skLineSegment(sketch, "E109", {"start": v(-41.5, 30) * mm, "end": v(-30.25, 30) * mm});
            skSolve(sketch);
        }
        {
            var Q0;
            Q0=makeQuery(id+"F29.imprint","IMPRINT",FACE,{"disambiguationData":[TD([[makeQuery(id+"F29.imprint","IMPRINT",EDGE,{"derivedFrom":sQuery(id+"F29.wireOp",EDGE,"E93")}),-1.0]])]});
            var Q1;
            {var subQ1=makeQuery(id+"F3.opExtrude","CAP_EDGE",EDGE,{"disambiguationData":[OSD([sQuery(id+"F2.wireOp",EDGE,"E6.MirrorCS")])],"isStart":true});Q1=makeQuery(id+"F29.imprint","IMPRINT",FACE,{"disambiguationData":[TD([[makeQuery(id+"F29.imprint","IMPRINT",EDGE,{"derivedFrom":subQ1}),1.0]])]});}
            var Q2;
            Q2=makeQuery(id+"F29.imprint","IMPRINT",FACE,{"disambiguationData":[TD([[makeQuery(id+"F29.imprint","IMPRINT",EDGE,{"derivedFrom":makeQuery(id+"F3.opExtrude","CAP_EDGE",EDGE,{"disambiguationData":[OSD([sQuery(id+"F2.wireOp",EDGE,"E5.bottom")])],"isStart":true})}),-1.0]])]});
            extrude(context, id + "F30", {"entities" : qUnion([Q0, Q1, Q2]), "operationType" : NewBodyOperationType.ADD, "depth" : 1.5 * mm});
        }
        {
            var Q0;
            Q0=makeQuery(id+"F25.opExtrude","CAP_FACE",FACE,{"disambiguationData":[OSD([sQuery(id+"F24.wireOp",EDGE,"E61.bottom"),sQuery(id+"F24.wireOp",EDGE,"E61.top"),sQuery(id+"F24.wireOp",EDGE,"E61.left"),sQuery(id+"F24.wireOp",EDGE,"E61.right"),sQuery(id+"F24.wireOp",EDGE,"E62.bottom"),sQuery(id+"F24.wireOp",EDGE,"E62.top"),sQuery(id+"F24.wireOp",EDGE,"E62.left"),sQuery(id+"F24.wireOp",EDGE,"E62.right"),sQuery(id+"F24.wireOp",EDGE,"E69.left"),sQuery(id+"F24.wireOp",EDGE,"E69.top"),sQuery(id+"F24.wireOp",EDGE,"E69.right"),sQuery(id+"F24.wireOp",EDGE,"E69.bottom"),sQuery(id+"F24.wireOp",EDGE,"E77"),sQuery(id+"F24.wireOp",EDGE,"E78"),sQuery(id+"F24.wireOp",EDGE,"E80"),sQuery(id+"F24.wireOp",EDGE,"E81"),sQuery(id+"F24.wireOp",EDGE,"E83"),sQuery(id+"F24.wireOp",EDGE,"E87")])],"isStart":true});
            var sketch = newSketch(context, id + "F31", { "sketchPlane" : qUnion([Q0])});
            skLineSegment(sketch, "E110.bottom", {"start": v(-22.5, 63.9) * mm, "end": v(22.5, 63.9) * mm});
            skLineSegment(sketch, "E110.top", {"start": v(-22.5, 60.4) * mm, "end": v(22.5, 60.4) * mm});
            skLineSegment(sketch, "E110.left", {"start": v(-22.5, 63.9) * mm, "end": v(-22.5, 60.4) * mm});
            skLineSegment(sketch, "E110.right", {"start": v(22.5, 63.9) * mm, "end": v(22.5, 60.4) * mm});
            skLineSegment(sketch, "E111.0", {"start": v(64, 64.2) * mm, "end": v(64, 56.2) * mm, "construction": true});
            skLineSegment(sketch, "E112.0", {"start": v(-64, 64.2) * mm, "end": v(-64, 56.2) * mm, "construction": true});
            skLineSegment(sketch, "E113", {"start": v(64, 60.2) * mm, "end": v(22.5, 60.4) * mm, "construction": true});
            skLineSegment(sketch, "E114", {"start": v(-22.5, 60.4) * mm, "end": v(-64, 60.4) * mm, "construction": true});
            skLineSegment(sketch, "E115.0", {"start": v(64, 3.5) * mm, "end": v(-64, 3.5) * mm, "construction": true});
            skLineSegment(sketch, "E116.bottom", {"start": v(22.5, 3.65) * mm, "end": v(-22.5, 3.65) * mm});
            skLineSegment(sketch, "E116.top", {"start": v(22.5, 9.14) * mm, "end": v(-22.5, 9.14) * mm});
            skLineSegment(sketch, "E116.left", {"start": v(22.5, 3.65) * mm, "end": v(22.5, 9.14) * mm});
            skLineSegment(sketch, "E116.right", {"start": v(-22.5, 3.65) * mm, "end": v(-22.5, 9.14) * mm});
            skLineSegment(sketch, "E117", {"start": v(22.5, 60.4) * mm, "end": v(22.5, 9.14) * mm, "construction": true});
            skSolve(sketch);
        }
        {
            var Q0;
            Q0=makeQuery(id+"F31.imprint","IMPRINT",FACE,{"disambiguationData":[TD([[makeQuery(id+"F31.imprint","IMPRINT",EDGE,{"derivedFrom":sQuery(id+"F31.wireOp",EDGE,"E110.bottom")}),-1.0]])]});
            extrude(context, id + "F32", {"entities" : qUnion([Q0]), "operationType" : NewBodyOperationType.ADD, "depth" : 5 * mm});
        }
        {
            var Q0;
            Q0=makeQuery(id+"F8.opExtrude","SWEPT_FACE",FACE,{"disambiguationData":[OSD([sQuery(id+"F7.wireOp",EDGE,"E22")])]});
            var sketch = newSketch(context, id + "F33", { "sketchPlane" : qUnion([Q0])});
            skLineSegment(sketch, "E118.bottom", {"start": v(-75, 20) * mm, "end": v(75, 20) * mm});
            skLineSegment(sketch, "E118.top", {"start": v(-75, 45) * mm, "end": v(75, 45) * mm});
            skLineSegment(sketch, "E118.left", {"start": v(-75, 20) * mm, "end": v(-75, 45) * mm});
            skLineSegment(sketch, "E118.right", {"start": v(75, 20) * mm, "end": v(75, 45) * mm});
            skLineSegment(sketch, "E119.bottom", {"start": v(-42, 30) * mm, "end": v(42, 30) * mm});
            skLineSegment(sketch, "E119.top", {"start": v(-42, 45) * mm, "end": v(42, 45) * mm});
            skLineSegment(sketch, "E119.left", {"start": v(-42, 30) * mm, "end": v(-42, 45) * mm});
            skLineSegment(sketch, "E119.right", {"start": v(42, 30) * mm, "end": v(42, 45) * mm});
            skSolve(sketch);
        }
        {
            var Q0;
            Q0=makeQuery(id+"F33.imprint","IMPRINT",FACE,{"disambiguationData":[TD([[makeQuery(id+"F33.imprint","IMPRINT",EDGE,{"derivedFrom":sQuery(id+"F33.wireOp",EDGE,"E118.bottom")}),1.0]])]});
            var Q1;
            Q1=makeQuery(id+"F33.imprint","IMPRINT",FACE,{"disambiguationData":[TD([[makeQuery(id+"F33.imprint","IMPRINT",EDGE,{"derivedFrom":sQuery(id+"F33.wireOp",EDGE,"E119.bottom")}),1.0]])]});
            var Q2;
            Q2=makeQuery(id+"F33.imprint","IMPRINT",FACE,{"disambiguationData":[TD([[makeQuery(id+"F33.imprint","IMPRINT",EDGE,{"derivedFrom":makeQuery(id+"F13.hole-2.boolean.opBoolean","COPY",EDGE,{"derivedFrom":makeQuery(id+"F13.hole-2.opRevolve","SWEPT_EDGE",EDGE,{"disambiguationData":[OSD([sQuery(id+"F13.hole-2.sketch.wireOp",EDGE,"csink_start_line_1"),sQuery(id+"F13.hole-2.sketch.wireOp",EDGE,"csink_start_line_2")])]})})}),1.0]])]});
            var Q3;
            Q3=makeQuery(id+"F33.imprint","IMPRINT",FACE,{"disambiguationData":[TD([[makeQuery(id+"F33.imprint","IMPRINT",EDGE,{"derivedFrom":makeQuery(id+"F13.hole-1.boolean.opBoolean","COPY",EDGE,{"derivedFrom":makeQuery(id+"F13.hole-1.opRevolve","SWEPT_EDGE",EDGE,{"disambiguationData":[OSD([sQuery(id+"F13.hole-1.sketch.wireOp",EDGE,"csink_start_line_1"),sQuery(id+"F13.hole-1.sketch.wireOp",EDGE,"csink_start_line_2")])]})})}),1.0]])]});
            var Q4;
            Q4=makeQuery(id+"F33.imprint","IMPRINT",FACE,{"disambiguationData":[TD([[makeQuery(id+"F33.imprint","IMPRINT",EDGE,{"derivedFrom":makeQuery(id+"F13.hole-0.boolean.opBoolean","COPY",EDGE,{"derivedFrom":makeQuery(id+"F13.hole-0.opRevolve","SWEPT_EDGE",EDGE,{"disambiguationData":[OSD([sQuery(id+"F13.hole-0.sketch.wireOp",EDGE,"csink_start_line_1"),sQuery(id+"F13.hole-0.sketch.wireOp",EDGE,"csink_start_line_2")])]})})}),1.0]])]});
            extrude(context, id + "F34", {"entities" : qUnion([Q0, Q1, Q2, Q3, Q4]), "depth" : 6 * mm});
        }
        {
            var Q0;
            Q0=makeQuery(id+"F33.imprint","IMPRINT",FACE,{"disambiguationData":[TD([[makeQuery(id+"F33.imprint","IMPRINT",EDGE,{"derivedFrom":sQuery(id+"F33.wireOp",EDGE,"E119.bottom")}),1.0]])]});
            var Q1;
            Q1=makeQuery(id+"F33.imprint","IMPRINT",FACE,{"disambiguationData":[TD([[makeQuery(id+"F33.imprint","IMPRINT",EDGE,{"derivedFrom":makeQuery(id+"F13.hole-2.boolean.opBoolean","COPY",EDGE,{"derivedFrom":makeQuery(id+"F13.hole-2.opRevolve","SWEPT_EDGE",EDGE,{"disambiguationData":[OSD([sQuery(id+"F13.hole-2.sketch.wireOp",EDGE,"csink_start_line_1"),sQuery(id+"F13.hole-2.sketch.wireOp",EDGE,"csink_start_line_2")])]})})}),1.0]])]});
            var Q2;
            Q2=makeQuery(id+"F33.imprint","IMPRINT",FACE,{"disambiguationData":[TD([[makeQuery(id+"F33.imprint","IMPRINT",EDGE,{"derivedFrom":makeQuery(id+"F13.hole-1.boolean.opBoolean","COPY",EDGE,{"derivedFrom":makeQuery(id+"F13.hole-1.opRevolve","SWEPT_EDGE",EDGE,{"disambiguationData":[OSD([sQuery(id+"F13.hole-1.sketch.wireOp",EDGE,"csink_start_line_1"),sQuery(id+"F13.hole-1.sketch.wireOp",EDGE,"csink_start_line_2")])]})})}),1.0]])]});
            var Q3;
            Q3=makeQuery(id+"F33.imprint","IMPRINT",FACE,{"disambiguationData":[TD([[makeQuery(id+"F33.imprint","IMPRINT",EDGE,{"derivedFrom":makeQuery(id+"F13.hole-0.boolean.opBoolean","COPY",EDGE,{"derivedFrom":makeQuery(id+"F13.hole-0.opRevolve","SWEPT_EDGE",EDGE,{"disambiguationData":[OSD([sQuery(id+"F13.hole-0.sketch.wireOp",EDGE,"csink_start_line_1"),sQuery(id+"F13.hole-0.sketch.wireOp",EDGE,"csink_start_line_2")])]})})}),1.0]])]});
            extrude(context, id + "F35", {"entities" : qUnion([Q0, Q1, Q2, Q3]), "operationType" : NewBodyOperationType.REMOVE, "depth" : 4.4 * mm});
        }
        {
            var Q0;
            Q0=makeQuery(id+"F34.opExtrude","SWEPT_FACE",FACE,{"disambiguationData":[OSD([sQuery(id+"F33.wireOp",EDGE,"E118.right")])]});
            var sketch = newSketch(context, id + "F36", { "sketchPlane" : qUnion([Q0])});
            skFitSpline(sketch, "E120", {"points": [v(20, 67.2) * mm, v(24.56, 70.06) * mm, v(28.97, 73.2) * mm], "startDerivative": vector(14.72, 0) * mm, "endDerivative": vector(12.47, 2) * mm});
            skLineSegment(sketch, "E121", {"start": v(28.97, 73.2) * mm, "end": v(20, 73.2) * mm});
            skLineSegment(sketch, "E122", {"start": v(20, 73.2) * mm, "end": v(20, 67.2) * mm});
            skSolve(sketch);
        }
        {
            var Q0;
            Q0=makeQuery(id+"F36.imprint","IMPRINT",FACE,{"disambiguationData":[TD([[makeQuery(id+"F36.imprint","IMPRINT",EDGE,{"derivedFrom":sQuery(id+"F36.wireOp",EDGE,"E120")}),1.0]])]});
            extrude(context, id + "F37", {"entities" : qUnion([Q0]), "operationType" : NewBodyOperationType.REMOVE, "endBound" : BoundingType.UP_TO_NEXT, "oppositeDirection" : true, "depth" : 25 * mm});
        }
        {
            var Q0;
            Q0=makeQuery(id+"F34.opExtrude","CAP_FACE",FACE,{"disambiguationData":[OSD([sQuery(id+"F33.wireOp",EDGE,"E118.bottom"),sQuery(id+"F33.wireOp",EDGE,"E118.top"),sQuery(id+"F33.wireOp",EDGE,"E118.left"),sQuery(id+"F33.wireOp",EDGE,"E118.right"),sQuery(id+"F33.wireOp",EDGE,"E119.top")])],"isStart":false});
            var sketch = newSketch(context, id + "F38", { "sketchPlane" : qUnion([Q0])});
            skCircle(sketch, "E123.0", {"center": v(25, 39.8) * mm, "radius": 1.55 * mm});
            skCircle(sketch, "E124.0", {"center": v(0, 39.8) * mm, "radius": 1.55 * mm});
            skCircle(sketch, "E125.0", {"center": v(-25, 39.8) * mm, "radius": 1.55 * mm});
            skSolve(sketch);
        }
        {
            var Q0;
            Q0=sQuery(id+"F38.wireOp",VERTEX,"E123.0.center");
            var Q1;
            Q1=sQuery(id+"F38.wireOp",VERTEX,"E124.0.center");
            var Q2;
            Q2=sQuery(id+"F38.wireOp",VERTEX,"E125.0.center");
            var Q3;
            Q3=makeQuery(id+"F34.opExtrude","SWEPT_BODY",BODY,{"disambiguationData":[OSD([sQuery(id+"F33.wireOp",EDGE,"E118.bottom"),sQuery(id+"F33.wireOp",EDGE,"E118.top"),sQuery(id+"F33.wireOp",EDGE,"E118.left"),sQuery(id+"F33.wireOp",EDGE,"E118.right"),sQuery(id+"F33.wireOp",EDGE,"E119.top")])]});
            hole(context, id + "F39", {"style" : HoleStyle.C_SINK, "holeDiameter" : 3.05 * mm, "cSinkDiameter" : 5.47 * mm, "endStyle" : HoleEndStyle.THROUGH, "locations" : qUnion([Q0, Q1, Q2]), "scope" : qUnion([Q3]), "cSinkAngle" : 90 * degree});
        }
    });
